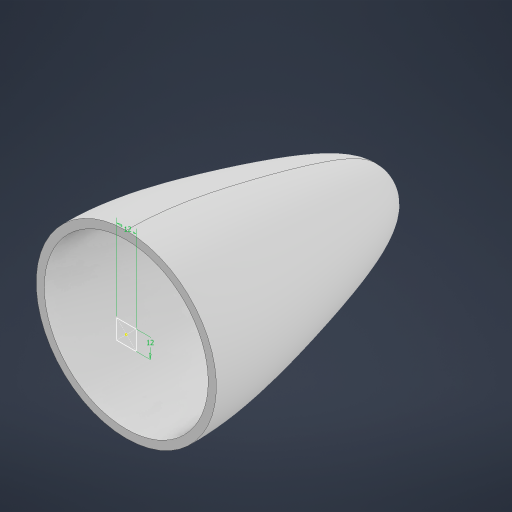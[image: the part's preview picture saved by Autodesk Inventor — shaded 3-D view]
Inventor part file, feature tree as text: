
AUTODESK INVENTOR PART (.ipt)
format: ipt  version: 2023.2 (Build 272271000, 271)  size: 499,200 bytes
history: native  units: mm
features: sketch x2, revolve x2, other x1, shell x1
ambient origin geometry x8: Origin, YZ Plane, XZ Plane, XY Plane, X Axis, Y Axis, Z Axis, Center Point
bodies: Volumenkörper1 (feature_tree), Volumenkörper2 (feature_tree)
feature tree (6):
  sketch  "Skizze4"  dims[d3=160.0mm]
  revolve  "Umdrehung1"
  revolve  "Umdrehung2"
  other  "Körper verschieben1"
  shell  "Wandung3"  Thickness=80.0mm
  sketch  "Skizze10"  dims[d4=360.0deg d5=360.0deg d6=0.0mm d7=0.0mm d8=50.0mm d11=5.0mm d22=12.0mm d23=12.0mm]
